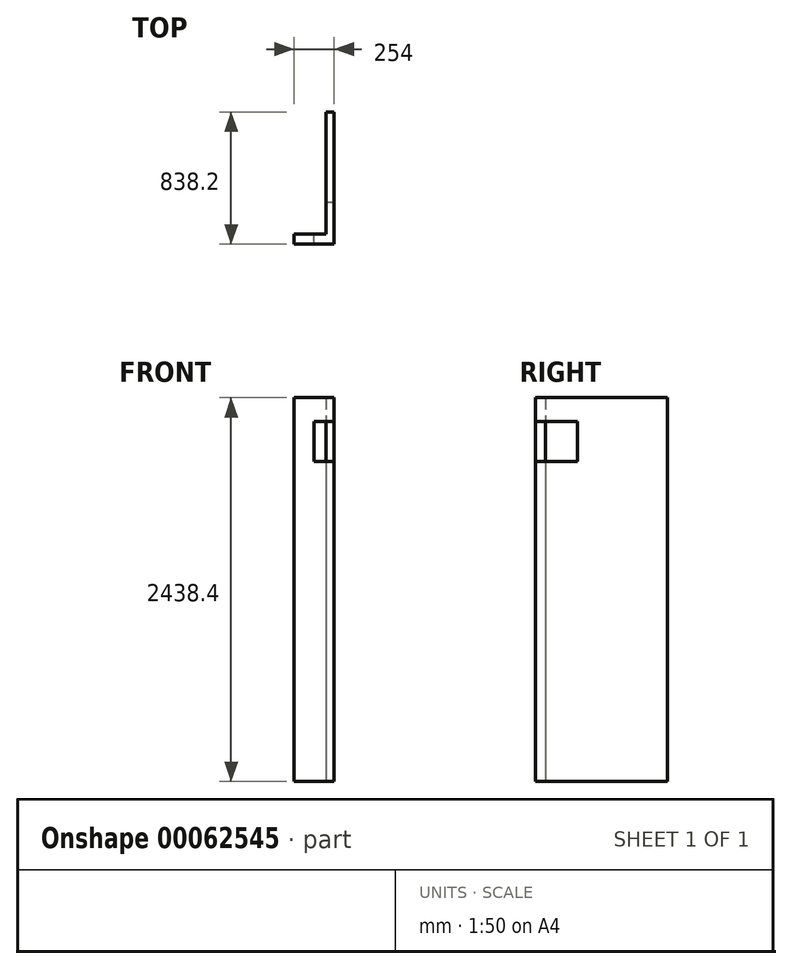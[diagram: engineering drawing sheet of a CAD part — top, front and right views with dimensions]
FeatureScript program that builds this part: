
annotation { "Feature Type Name" : "Feature", "Feature Type Description" : "" }
export const myFeature = defineFeature(function(context is Context, id is Id, definition is map)
    precondition{}
    {
        {
            var Q0;
            Q0=qCreatedBy(makeId("Right.planeOp"),FACE);
            var sketch = newSketch(context, id + "F0", { "sketchPlane" : qUnion([Q0])});
            skLineSegment(sketch, "E0.rect.bottom", {"start": v(419.1, 1219.2) * mm, "end": v(-419.1, 1219.2) * mm});
            skLineSegment(sketch, "E0.rect.top", {"start": v(419.1, -1219.2) * mm, "end": v(-419.1, -1219.2) * mm});
            skLineSegment(sketch, "E0.rect.left", {"start": v(419.1, 1219.2) * mm, "end": v(419.1, -1219.2) * mm});
            skLineSegment(sketch, "E0.rect.right", {"start": v(-419.1, 1219.2) * mm, "end": v(-419.1, -1219.2) * mm});
            skPoint(sketch, "E0.rect.middle", {"position": v(0, 0) * mm});
            skSolve(sketch);
        }
        {
            var Q0;
            Q0=qSketchRegion(id+"F0",true);
            extrude(context, id + "F1", {"entities" : qUnion([Q0]), "depth" : 50.8 * mm});
        }
        {
            var Q0;
            Q0=makeQuery(id+"F1.opExtrude","CAP_FACE",FACE,{"disambiguationData":[OSD([sQuery(id+"F0.wireOp",EDGE,"E0.rect.bottom"),sQuery(id+"F0.wireOp",EDGE,"E0.rect.top"),sQuery(id+"F0.wireOp",EDGE,"E0.rect.left"),sQuery(id+"F0.wireOp",EDGE,"E0.rect.right")])],"isStart":true});
            var sketch = newSketch(context, id + "F2", { "sketchPlane" : qUnion([Q0])});
            skLineSegment(sketch, "E1.bottom", {"start": v(419.1, 1219.2) * mm, "end": v(355.6, 1219.2) * mm});
            skLineSegment(sketch, "E1.top", {"start": v(419.1, -1219.2) * mm, "end": v(355.6, -1219.2) * mm});
            skLineSegment(sketch, "E1.left", {"start": v(419.1, 1219.2) * mm, "end": v(419.1, -1219.2) * mm});
            skLineSegment(sketch, "E1.right", {"start": v(355.6, 1219.2) * mm, "end": v(355.6, -1219.2) * mm});
            skSolve(sketch);
        }
        {
            var Q0;
            Q0=qSketchRegion(id+"F2",true);
            extrude(context, id + "F3", {"entities" : qUnion([Q0]), "operationType" : NewBodyOperationType.ADD, "depth" : 203.2 * mm});
        }
        {
            var Q0;
            Q0=makeQuery(id+"F3.boolean.opBoolean","MERGE",FACE,{"derivedFrom":[makeQuery(id+"F1.opExtrude","SWEPT_FACE",FACE,{"disambiguationData":[OSD([sQuery(id+"F0.wireOp",EDGE,"E0.rect.right")])]}),makeQuery(id+"F3.opExtrude","SWEPT_FACE",FACE,{"disambiguationData":[OSD([sQuery(id+"F2.wireOp",EDGE,"E1.left")])]})]});
            var sketch = newSketch(context, id + "F4", { "sketchPlane" : qUnion([Q0])});
            skLineSegment(sketch, "E2.bottom", {"start": v(50.8, 1066.8) * mm, "end": v(-101.6, 1066.8) * mm});
            skLineSegment(sketch, "E2.top", {"start": v(50.8, 812.8) * mm, "end": v(-101.6, 812.8) * mm});
            skLineSegment(sketch, "E2.left", {"start": v(50.8, 1066.8) * mm, "end": v(50.8, 812.8) * mm});
            skLineSegment(sketch, "E2.right", {"start": v(-101.6, 1066.8) * mm, "end": v(-101.6, 812.8) * mm});
            skSolve(sketch);
        }
        {
            var Q0;
            Q0=makeQuery(id+"FNlMqnm3bAsIZNR_1.boolean.opBoolean","MERGE",FACE,{"derivedFrom":[makeQuery(id+"F1.opExtrude","CAP_FACE",FACE,{"disambiguationData":[OSD([sQuery(id+"F0.wireOp",EDGE,"E0.rect.bottom"),sQuery(id+"F0.wireOp",EDGE,"E0.rect.top"),sQuery(id+"F0.wireOp",EDGE,"E0.rect.left"),sQuery(id+"F0.wireOp",EDGE,"E0.rect.right")])],"isStart":false}),makeQuery(id+"FNlMqnm3bAsIZNR_1.opExtrude","SWEPT_FACE",FACE,{"disambiguationData":[OSD([sQuery(id+"F4.wireOp",EDGE,"E2.left")])]})]});
            var sketch = newSketch(context, id + "F5", { "sketchPlane" : qUnion([Q0])});
            skLineSegment(sketch, "E3.bottom", {"start": v(-457.2, 1066.8) * mm, "end": v(-152.4, 1066.8) * mm});
            skLineSegment(sketch, "E3.top", {"start": v(-457.2, 812.8) * mm, "end": v(-152.4, 812.8) * mm});
            skLineSegment(sketch, "E3.left", {"start": v(-457.2, 1066.8) * mm, "end": v(-457.2, 812.8) * mm});
            skLineSegment(sketch, "E3.right", {"start": v(-152.4, 1066.8) * mm, "end": v(-152.4, 812.8) * mm});
            skSolve(sketch);
        }
        {
            var Q0;
            Q0=qSketchRegion(id+"F5",true);
            extrude(context, id + "F6", {"entities" : qUnion([Q0]), "operationType" : NewBodyOperationType.REMOVE, "oppositeDirection" : true, "depth" : 127 * mm});
        }
    });
